# Revit family: centriq_140-0650
name_source: partatom
category: Leuchten
revit_build: Autodesk Revit 2016 (Build: 20190508_0715(x64)
units: mm (PartAtom-declared; Revit-internal decimal feet)

## family parameters
Basisbauteil = Fläche
Beim Laden mit Abzugskörper schneiden = Nein
Bemaßung runder Anschluss = Durchmesser verwenden
Gemeinsam genutzt = Nein
Lichtquelle = Nein
Raumberechnungspunkt = Nein
Teiletyp = Normal

## types (1)
- 140-0650- (1 x LED, 447.88 lm, 6.3 W, 2700K)
    Beschreibung = CENTRIQ
    CIE Flux Codes = 99 100 100 100 82
    Color Rendering = 1A/90…99
    Color Temperature = 2700K
    Height = 99 mm
    Hersteller = Prolicht
    Lamp Light Flux = 447.88 lm
    Lamp Power = 6.3 W
    Lamp count = 1
    Lampe = 1 x LED
    Length = 38 mm
    Luminous efficacy = 58 lm/W
    ModVariant = Nein
    Modell = 140-0650
    Mounting Place = Ceiling
    Mounting Type = Surface mounted
    Number of Poles = 1
    OnlyDefault = Ja
    Power Factor = 1
    Product Name = CENTRIQ
    Product group = Surface track spotlights
    ProductGroupID = 333
    Protection Class = Protection class
    Protection Degree = Degree of protection
    RLX_Detail_Level = 1
    RlxData = <blob elided: 282785 chars, md5=5b994b08>
    Scheinlast = 6 VA
    Socket = socket
    Standby Power = 0 W
    System Light Flux = 368 lm
    System Power = 6 W
    Typenbild = 140-0650.jpg
    URL = http://relux.com
    VarID = 140-0650-
    Voltage = 0 V
    Vorgabe-Ansicht = 1800 mm
    Weight = 0.00 kg
    Width = 0 mm  [stored 0 ft]

note: [stored X ft] marks values corroborated as IEEE doubles in the binary element streams (Revit-internal decimal feet)

## geometry (parser evidence)
native form markers: Blend x4, Sweep x15
no freeform markers — native parametric forms only
